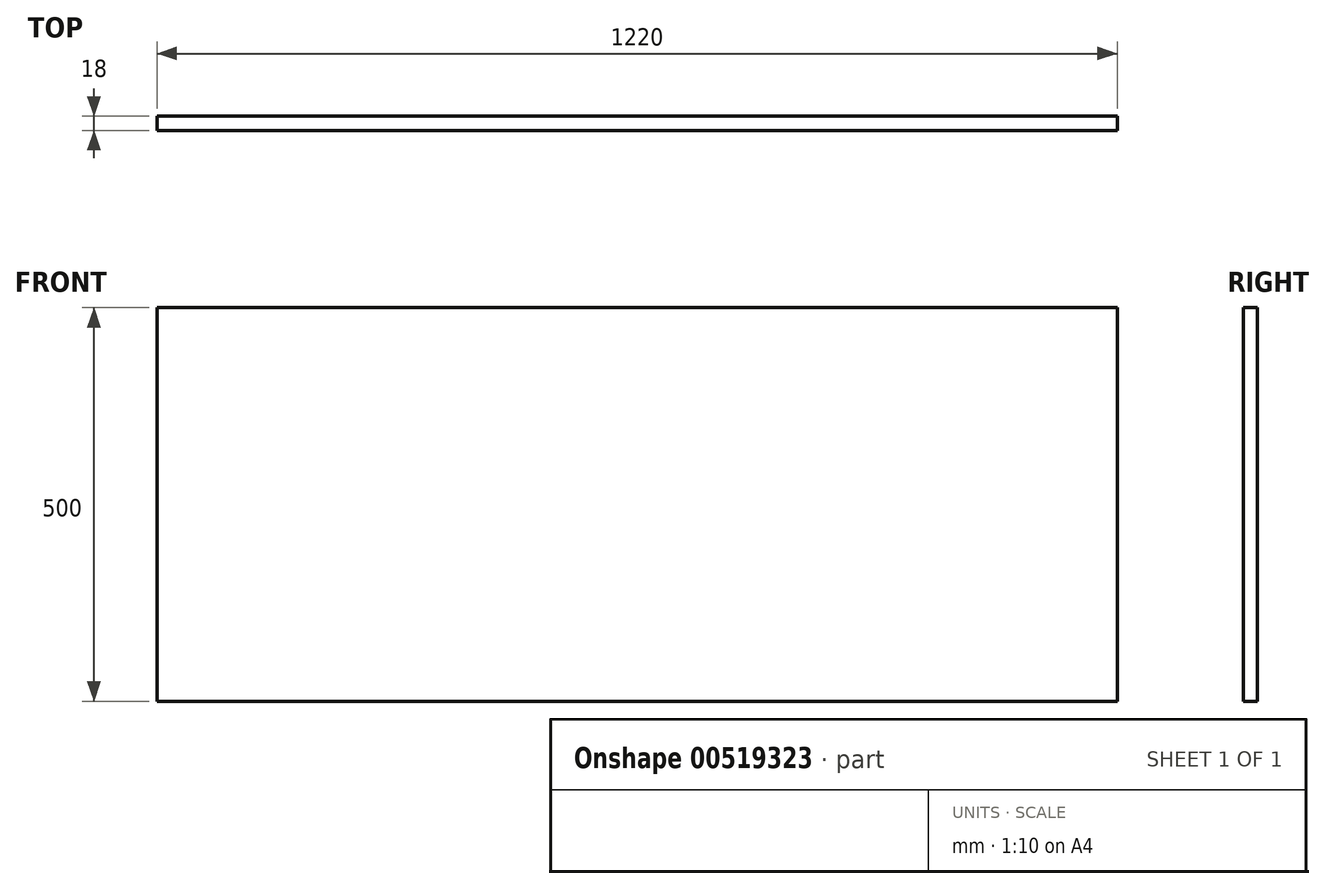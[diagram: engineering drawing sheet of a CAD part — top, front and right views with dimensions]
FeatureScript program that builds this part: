
annotation { "Feature Type Name" : "Feature", "Feature Type Description" : "" }
export const myFeature = defineFeature(function(context is Context, id is Id, definition is map)
    precondition{}
    {
        {
            var Q0;
            Q0=qCreatedBy(makeId("Front.planeOp"),FACE);
            var sketch = newSketch(context, id + "F0", { "sketchPlane" : qUnion([Q0])});
            skLineSegment(sketch, "E0.bottom", {"start": v(610, 250) * mm, "end": v(-610, 250) * mm});
            skLineSegment(sketch, "E0.top", {"start": v(610, -250) * mm, "end": v(-610, -250) * mm});
            skLineSegment(sketch, "E0.left", {"start": v(610, 250) * mm, "end": v(610, -250) * mm});
            skLineSegment(sketch, "E0.right", {"start": v(-610, 250) * mm, "end": v(-610, -250) * mm});
            skPoint(sketch, "E0.middle", {"position": v(0, 0) * mm});
            skSolve(sketch);
        }
        {
            var Q0;
            Q0=makeQuery(id+"F0.imprint","IMPRINT",FACE,{"disambiguationData":[TD([[makeQuery(id+"F0.imprint","IMPRINT",EDGE,{"derivedFrom":sQuery(id+"F0.wireOp",EDGE,"E0.bottom")}),1.0]])]});
            extrude(context, id + "F1", {"entities" : qUnion([Q0]), "depth" : 18 * mm, "offsetDistance" : 25 * mm});
        }
    });
